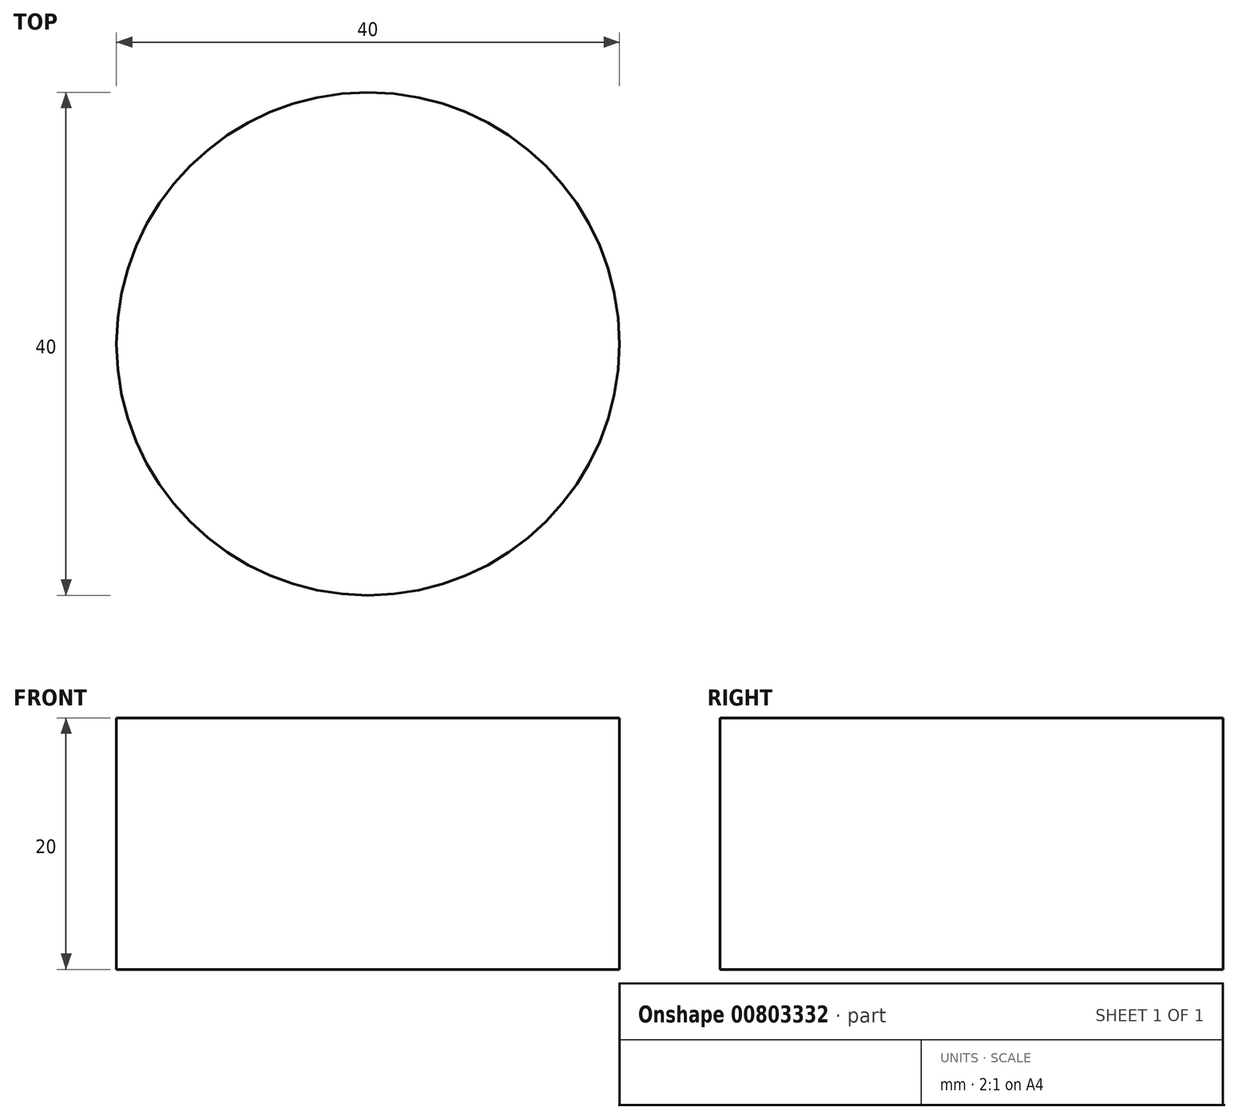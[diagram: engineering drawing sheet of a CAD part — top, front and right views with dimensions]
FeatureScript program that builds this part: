
annotation { "Feature Type Name" : "Feature", "Feature Type Description" : "" }
export const myFeature = defineFeature(function(context is Context, id is Id, definition is map)
    precondition{}
    {
        {
            var Q0;
            Q0=qCreatedBy(makeId("Top.planeOp"),FACE);
            var sketch = newSketch(context, id + "F0", { "sketchPlane" : qUnion([Q0])});
            skCircle(sketch, "E0", {"center": v(0, 0) * mm, "radius": 20 * mm});
            skSolve(sketch);
        }
        {
            var Q0;
            Q0 = qSketchRegion(id + "F0", true);
            extrude(context, id + "F1", {"entities" : qUnion([Q0]), "depth" : 20 * mm, "offsetDistance" : 25 * mm});
        }
    });
